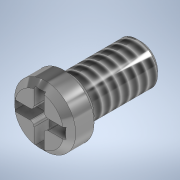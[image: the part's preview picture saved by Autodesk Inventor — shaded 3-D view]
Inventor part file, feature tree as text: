
AUTODESK INVENTOR PART (.ipt)
format: ipt  version: 2021 (Build 250183000, 183)  size: 169,472 bytes
history: native  units: mm
features: extrude x3, sketch x3, chamfer x2, other x1, thread x1, fillet x1
ambient origin geometry x8: Origin, YZ Plane, XZ Plane, XY Plane, X Axis, Y Axis, Z Axis, Center Point
bodies: Body1 (feature_tree)
feature tree (11):
  other  "Sólido1"
  extrude  "Extrusão1"  Depth=3.5mm TaperAngle=0.0deg
  extrude  "Extrusão2"  Depth=1.5mm TaperAngle=0.0deg
  extrude  "Extrusão3"  Depth=0.5mm
  thread  "Rosca1"  [1 undecoded]
  fillet  "Arredondamento3"  Radius=0.5mm
  chamfer  "Chanfro1"  Distance=0.75mm
  chamfer  "Chanfro2"  Distance=5.0mm
  sketch  "Esboço1"  dims[d0=2.031mm d1=3.5mm d2=0.0mm]
  sketch  "Esboço2"  dims[d3=3.0mm d4=1.5mm d5=0.0mm]
  sketch  "Esboço3"  dims[d6=0.5mm d7=2.5mm d8=2.5mm d9=0.5mm d10=0.75mm d11=0.0mm d14=5.0mm d15=0.0mm d16=0.2mm d17=0.3mm d18=2.0mm d19=45.0deg d20=0.2mm d21=2.0mm d22=45.0deg]
note: 1 required parameter value undecoded (feature->parameter linkage not recoverable at this tier; creation-order binding heuristic only, values carry confidence <= 0.55)
